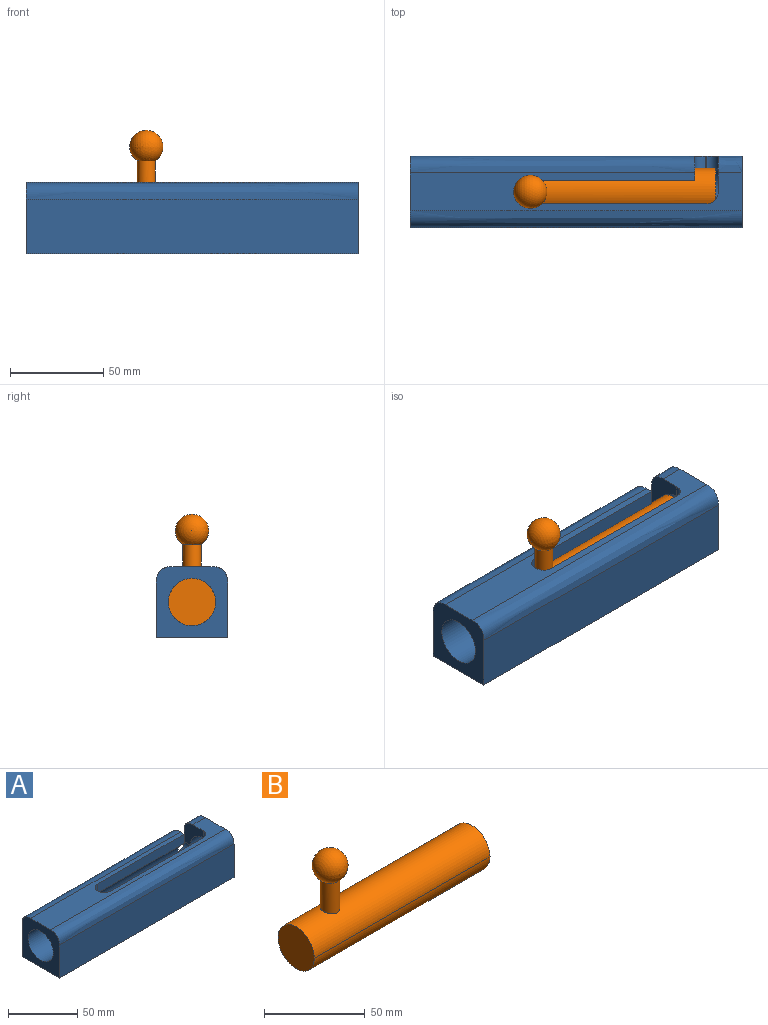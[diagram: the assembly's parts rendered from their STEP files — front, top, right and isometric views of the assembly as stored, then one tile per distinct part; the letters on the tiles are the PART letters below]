
ASSEMBLY  parts=2 mates=1
PART A: 21 faces, bbox 195.6x38.1x38.1 mm
  f0: plane 177.8x20.32mm, normal (0,0,1), area 2230.7mm2, adj f2,f4,f7,f8,f9,f10,f11,f13
  f1: cylinder r=12.7mm len=177.8mm, axis (-1,0,0), area 12556.3mm2, adj f2,f4,f7,f8,f9,f10,f11,f12
  f2: plane 38.1x38.1mm, normal (-1,0,0), area 918.6mm2, adj f0,f1,f3,f5,f6,f19,f20
  f3: plane 177.8x38.1mm, normal (0,0,-1), area 6774.2mm2, adj f2,f4,f5,f6
  f4: plane 38.1x38.1mm, normal (1,0,0), area 918.6mm2, adj f0,f1,f3,f5,f6,f18,f20
  f5: plane 177.8x29.21mm, normal (0,-1,0), area 5193.5mm2, adj f2,f3,f4,f20
  f6: plane 177.8x29.21mm, normal (0,1,0), area 4999.8mm2, adj f2,f3,f4,f7,f8,f12,f16,f17
  f7: plane 19.3x19.3mm, normal (-1,0,0), area 226.3mm2, adj f0,f1,f6,f15,f16,f18
  f8: plane 19.3x12.7mm, normal (1,0,0), area 180.8mm2, adj f0,f1,f6,f9,f17,f19
  f9: plane 88.11x8.05mm, normal (0,-1,0), area 709.4mm2, adj f0,f1,f8,f13
  f10: plane 6.35x0.51mm, normal (1,0,0), area 3.2mm2, adj f0,f1,f13,f14
  f11: plane 94.71x8.05mm, normal (0,1,0), area 762.6mm2, adj f0,f1,f14,f15
  f12: plane 8.05x0.51mm, normal (0,0,1), area 4.1mm2, adj f1,f6,f16,f17
  f13: cylinder r=6.1mm len=8.05mm, axis (0,0,1), area 69mm2, adj f0,f1,f9,f10
  f14: cylinder r=6.1mm len=8.05mm, axis (0,0,-1), area 69mm2, adj f0,f1,f10,f11
  f15: cylinder r=6.1mm len=8.05mm, axis (0,0,1), area 69mm2, adj f0,f1,f7,f11
  f16: cylinder r=6.1mm len=8.05mm, axis (0,1,0), area 69mm2, adj f1,f6,f7,f12
  f17: cylinder r=6.1mm len=8.05mm, axis (0,-1,0), area 69mm2, adj f1,f6,f8,f12
  f18: bspline ~13.97x8.89mm, area 183.3mm2, adj f0,f4,f6,f7
  f19: bspline ~167.64x8.89mm, area 2199.2mm2, adj f0,f2,f6,f8
  f20: bspline ~195.58x8.89mm, area 2565.7mm2, adj f0,f2,f4,f5
PART B: 6 faces, bbox 123.2x25.4x63.5 mm
  f0: cylinder r=12.7mm len=123.19mm, axis (-1,0,0), area 4840mm2, adj f1,f2,f3,f4
  f1: extruded ~123.19x25.4mm, area 4915.1mm2, adj f0,f2,f3
  f2: plane 29.21x25.4mm, normal (1,0,0), area 506.7mm2, adj f0,f1
  f3: plane 29.21x25.4mm, normal (-1,0,0), area 506.7mm2, adj f0,f1
  f4: cylinder r=4.84mm len=18.89mm, axis (0,0,-1), area 560.3mm2, adj f0,f5
  f5: sphere r=8.9mm, area 915.5mm2, adj f4
PLACE A t=(0,13.83,-26.09)mm fixed
PLACE B rot(axis=(1,0,0),0deg) t=(-13.51,14.44,-69.01)mm
MATE cylindrical A.f1 <-> B.f0  axis (-1,0,0) through (34.75,-5.22,-31.04)mm
